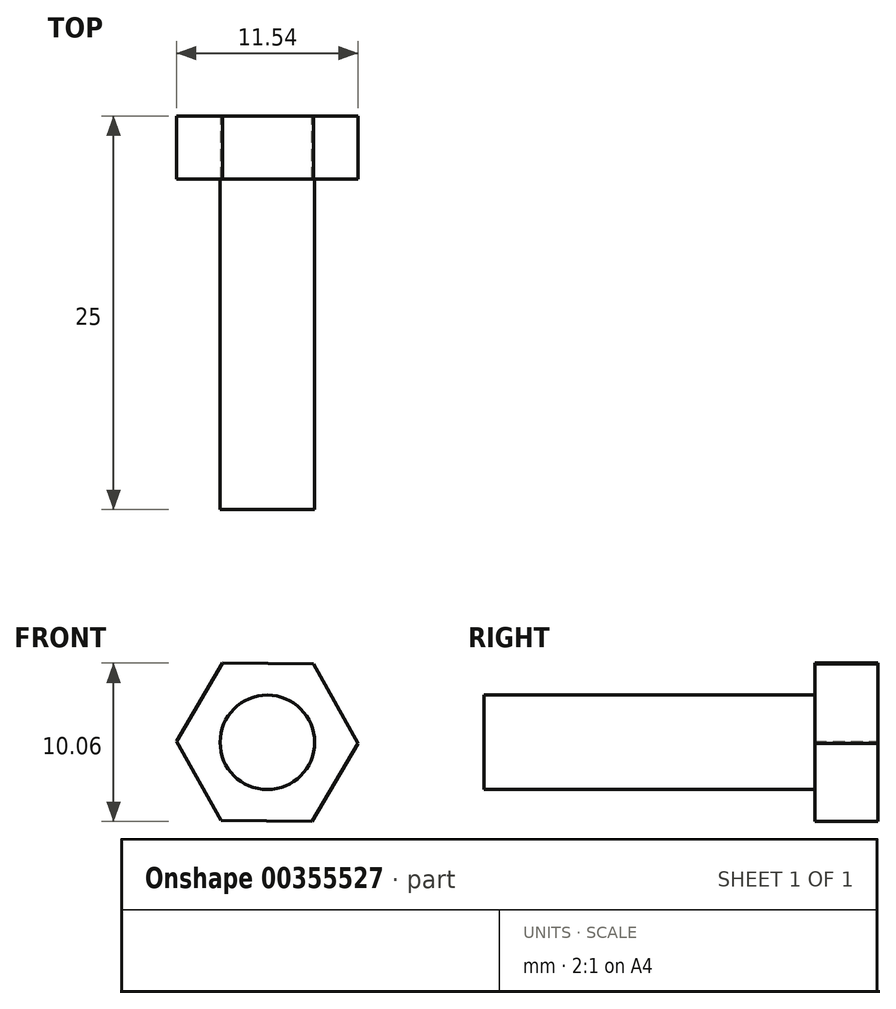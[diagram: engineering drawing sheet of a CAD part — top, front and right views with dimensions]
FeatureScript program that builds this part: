
annotation { "Feature Type Name" : "Feature", "Feature Type Description" : "" }
export const myFeature = defineFeature(function(context is Context, id is Id, definition is map)
    precondition{}
    {
        {
            var Q0;
            Q0=qCreatedBy(makeId("Front.planeOp"),FACE);
            var sketch = newSketch(context, id + "F0", { "sketchPlane" : qUnion([Q0])});
            skCircle(sketch, "E0", {"center": v(0, 0) * mm, "radius": 5 * mm});
            skSolve(sketch);
        }
        {
            var Q0;
            Q0 = qSketchRegion(id + "F0", true);
            extrude(context, id + "F1", {"entities" : qUnion([Q0]), "oppositeDirection" : true, "depth" : 25 * mm});
        }
        {
            var Q0;
            Q0=makeQuery(id+"F1.opExtrude","CAP_FACE",FACE,{"disambiguationData":[OSD([sQuery(id+"F0.wireOp",EDGE,"E0")])],"isStart":true});
            var sketch = newSketch(context, id + "F2", { "sketchPlane" : qUnion([Q0])});
            skCircle(sketch, "E1", {"center": v(0, 0) * mm, "radius": 7.16 * mm});
            skCircle(sketch, "E2", {"center": v(0, 0) * mm, "radius": 3 * mm});
            skSolve(sketch);
        }
        {
            var Q0;
            Q0=makeQuery(id+"F2.imprint","IMPRINT",FACE,{"disambiguationData":[TD([[makeQuery(id+"F2.imprint","IMPRINT",EDGE,{"derivedFrom":sQuery(id+"F2.wireOp",EDGE,"E2")}),-1.0]])]});
            extrude(context, id + "F3", {"entities" : qUnion([Q0]), "operationType" : NewBodyOperationType.REMOVE, "oppositeDirection" : true, "depth" : 21 * mm});
        }
        {
            var Q0;
            Q0=makeQuery(id+"F1.opExtrude","CAP_FACE",FACE,{"disambiguationData":[OSD([sQuery(id+"F0.wireOp",EDGE,"E0")])],"isStart":false});
            var sketch = newSketch(context, id + "F4", { "sketchPlane" : qUnion([Q0])});
            skCircle(sketch, "E3.cCircle", {"center": v(0, 0) * mm, "radius": 5 * mm, "construction": true});
            skLineSegment(sketch, "E3.0", {"start": v(5.77, 0.06) * mm, "end": v(2.94, -4.97) * mm});
            skLineSegment(sketch, "E3.1", {"start": v(2.94, -4.97) * mm, "end": v(-2.84, -5.03) * mm});
            skLineSegment(sketch, "E3.2", {"start": v(-2.84, -5.03) * mm, "end": v(-5.77, -0.06) * mm});
            skLineSegment(sketch, "E3.3", {"start": v(-5.77, -0.06) * mm, "end": v(-2.94, 4.97) * mm});
            skLineSegment(sketch, "E3.4", {"start": v(-2.94, 4.97) * mm, "end": v(2.84, 5.03) * mm});
            skLineSegment(sketch, "E3.5", {"start": v(2.84, 5.03) * mm, "end": v(5.77, 0.06) * mm});
            skPoint(sketch, "E3.0.midPoint", {"position": v(4.35, -2.46) * mm});
            skSolve(sketch);
        }
        {
            var Q0;
            Q0 = qSketchRegion(id + "F4", true);
            extrude(context, id + "F5", {"entities" : qUnion([Q0]), "operationType" : NewBodyOperationType.ADD, "oppositeDirection" : true, "depth" : 4 * mm});
        }
    });
